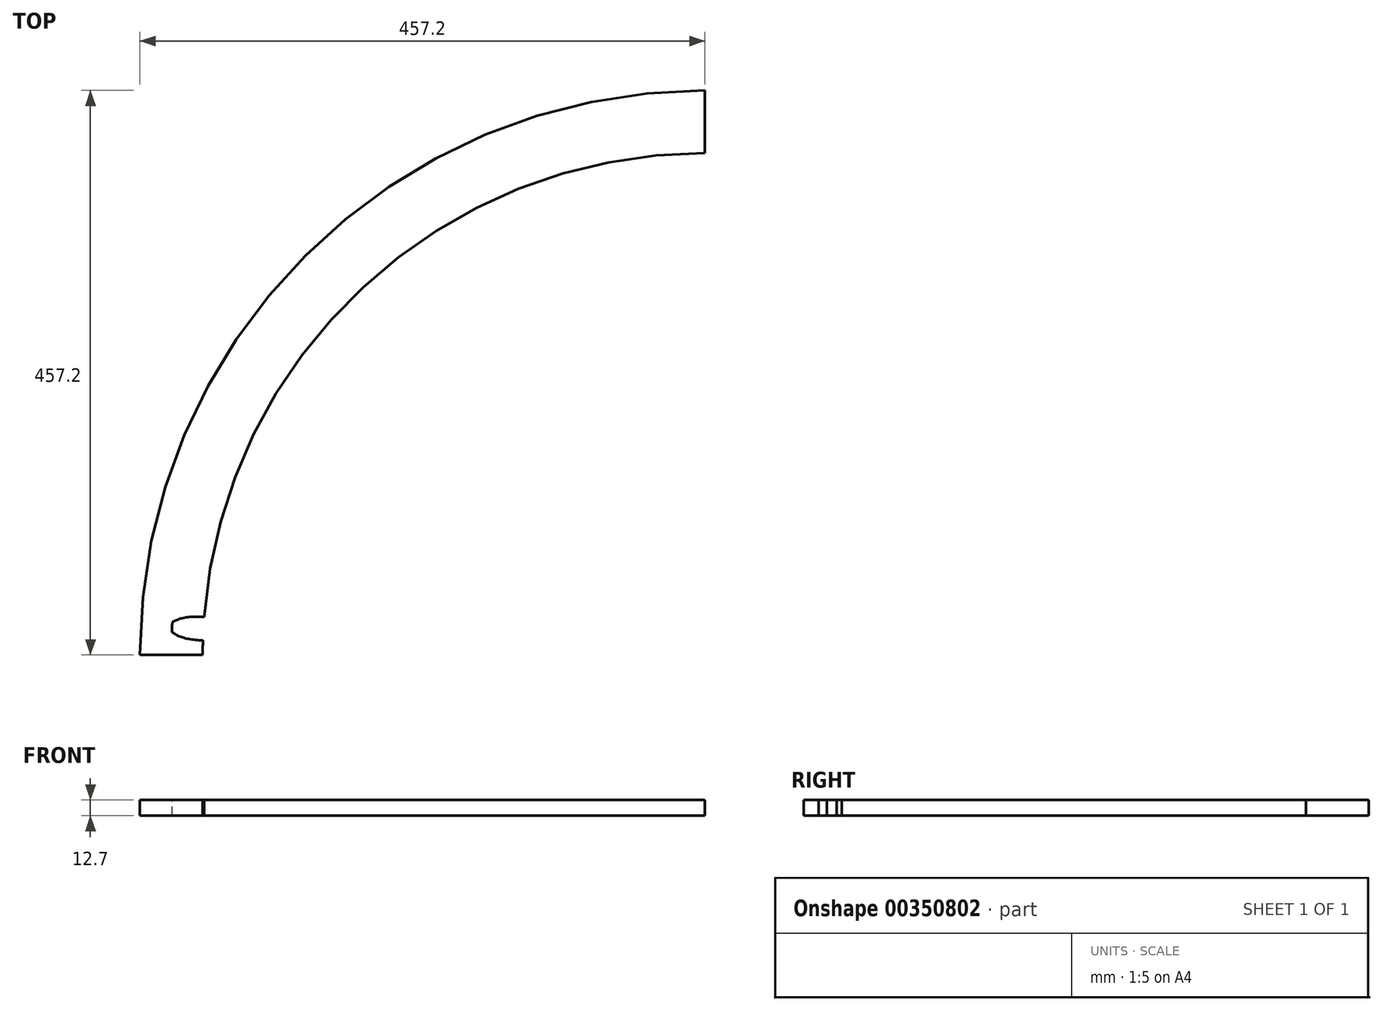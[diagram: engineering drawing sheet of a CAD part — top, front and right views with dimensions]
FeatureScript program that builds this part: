
annotation { "Feature Type Name" : "Feature", "Feature Type Description" : "" }
export const myFeature = defineFeature(function(context is Context, id is Id, definition is map)
    precondition{}
    {
        {
            var Q0;
            Q0=qCreatedBy(makeId("Top.planeOp"),FACE);
            var sketch = newSketch(context, id + "F0", { "sketchPlane" : qUnion([Q0])});
            skArc(sketch, "E0", {"start": v(0, 457.2) * mm, "mid": v(-323.29, 323.29) * mm, "end": v(-457.2, 0) * mm});
            skLineSegment(sketch, "E1", {"start": v(-457.2, 0) * mm, "end": v(-406.4, 0) * mm});
            skLineSegment(sketch, "E2", {"start": v(0, 457.2) * mm, "end": v(0, 406.4) * mm});
            skLineSegment(sketch, "E3", {"start": v(-406.4, 0) * mm, "end": v(0, 0) * mm, "construction": true});
            skLineSegment(sketch, "E4", {"start": v(0, 406.4) * mm, "end": v(0, 0) * mm, "construction": true});
            skArc(sketch, "E5", {"start": v(0, 406.4) * mm, "mid": v(-287.37, 287.37) * mm, "end": v(-406.4, 0) * mm});
            skSolve(sketch);
        }
        {
            var Q0;
            Q0 = qSketchRegion(id + "F0", true);
            extrude(context, id + "F1", {"entities" : qUnion([Q0]), "depth" : 12.7 * mm});
        }
        {
            var Q0;
            Q0=makeQuery(id+"F1.opExtrude","CAP_FACE",FACE,{"disambiguationData":[OSD([sQuery(id+"F0.wireOp",EDGE,"E0"),sQuery(id+"F0.wireOp",EDGE,"E1"),sQuery(id+"F0.wireOp",EDGE,"E2"),sQuery(id+"F0.wireOp",EDGE,"E5")])],"isStart":false});
            var sketch = newSketch(context, id + "F2", { "sketchPlane" : qUnion([Q0])});
            skLineSegment(sketch, "E6", {"start": v(0, 0) * mm, "end": v(-456.57, 23.93) * mm, "construction": true});
            skArc(sketch, "E7", {"start": v(-431.4, 18.64) * mm, "mid": v(-431.3, 20.62) * mm, "end": v(-431.2, 22.6) * mm});
            skArc(sketch, "E8", {"start": v(-406.23, 11.89) * mm, "mid": v(-406.06, 16.58) * mm, "end": v(-405.84, 21.27) * mm});
            skPoint(sketch, "E9.orphan", {"position": v(-431.8, 0) * mm});
            skFitSpline(sketch, "E10", {"points": [v(-431.4, 18.64) * mm, v(-427.02, 15.92) * mm, v(-417.88, 12.97) * mm, v(-406.23, 11.89) * mm], "startDerivative": vector(13.73, -10.24) * mm, "endDerivative": vector(22.59, 0.82) * mm});
            skArc(sketch, "E11.MirrorCS", {"start": v(-405.24, 30.64) * mm, "mid": v(-405.57, 25.96) * mm, "end": v(-405.84, 21.27) * mm});
            skFitSpline(sketch, "E12.MirrorCS", {"points": [v(-430.98, 26.55) * mm, v(-426.34, 28.8) * mm, v(-416.95, 30.78) * mm, v(-405.24, 30.64) * mm], "startDerivative": vector(14.73, 8.75) * mm, "endDerivative": vector(22.38, -3.18) * mm});
            skArc(sketch, "E13.MirrorCS", {"start": v(-430.98, 26.55) * mm, "mid": v(-431.1, 24.58) * mm, "end": v(-431.2, 22.6) * mm});
            skSolve(sketch);
        }
        {
            var Q0;
            Q0 = qSketchRegion(id + "F2", true);
            extrude(context, id + "F3", {"entities" : qUnion([Q0]), "operationType" : NewBodyOperationType.REMOVE, "endBound" : BoundingType.THROUGH_ALL, "oppositeDirection" : true, "depth" : 25.4 * mm});
        }
        {
            var Q0;
            Q0=qCreatedBy(makeId("Right.planeOp"),FACE);
            var sketch = newSketch(context, id + "F4", { "sketchPlane" : qUnion([Q0])});
            skLineSegment(sketch, "E14", {"start": v(0, 0) * mm, "end": v(0, 427.04) * mm, "construction": true});
            skSolve(sketch);
        }
    });
